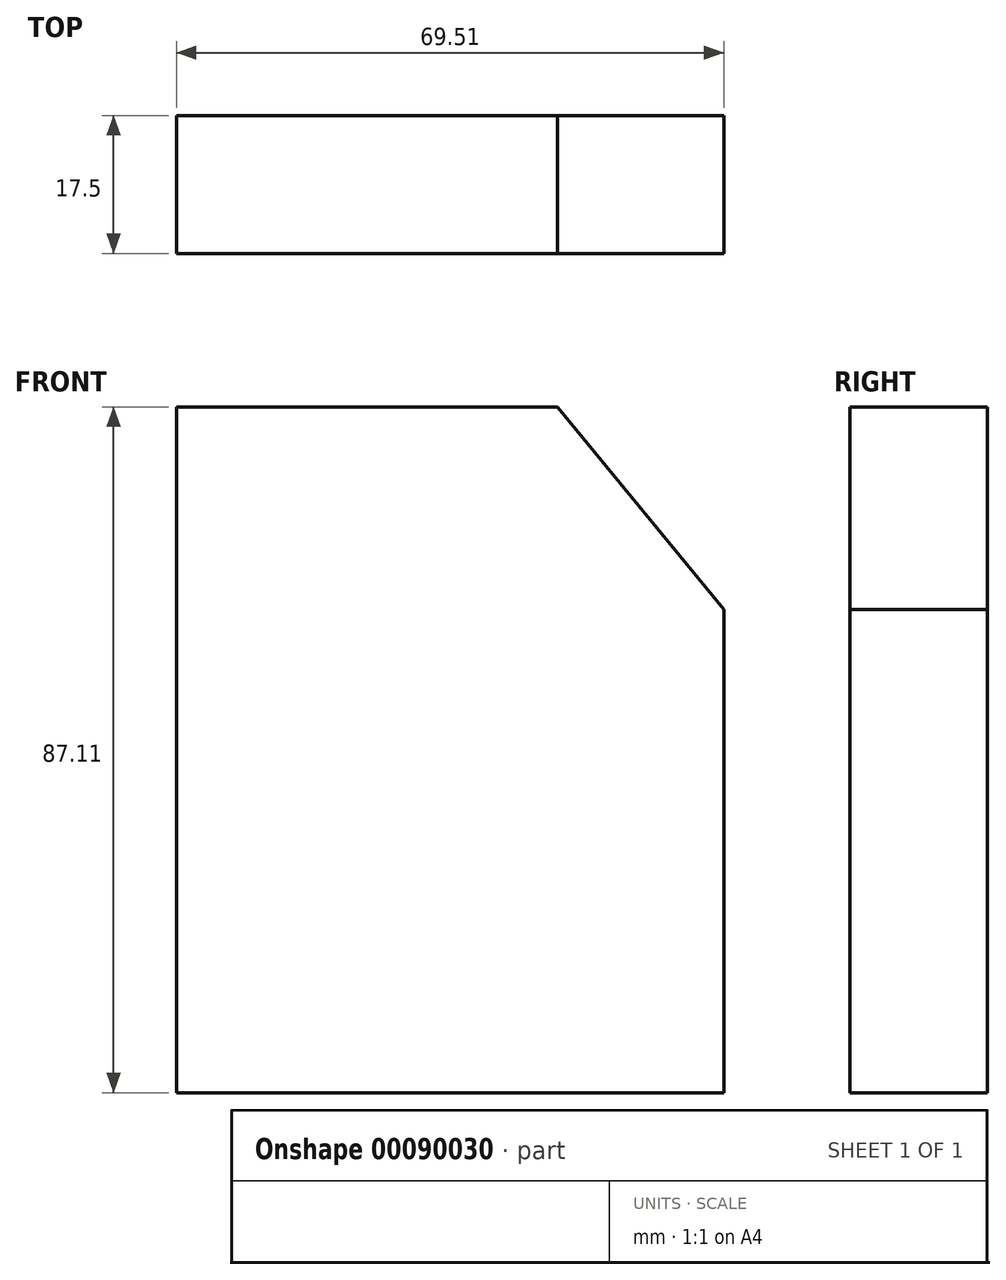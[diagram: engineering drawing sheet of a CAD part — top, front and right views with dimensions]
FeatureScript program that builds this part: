
annotation { "Feature Type Name" : "Feature", "Feature Type Description" : "" }
export const myFeature = defineFeature(function(context is Context, id is Id, definition is map)
    precondition{}
    {
        {
            var Q0;
            Q0=qCreatedBy(makeId("Front.planeOp"),FACE);
            var sketch = newSketch(context, id + "F0", { "sketchPlane" : qUnion([Q0])});
            skLineSegment(sketch, "E0.bottom", {"start": v(-22.88, -50) * mm, "end": v(46.63, -50) * mm});
            skLineSegment(sketch, "E0.top", {"start": v(-22.88, 37.1) * mm, "end": v(46.63, 37.1) * mm});
            skLineSegment(sketch, "E0.left", {"start": v(-22.88, -50) * mm, "end": v(-22.88, 37.1) * mm});
            skLineSegment(sketch, "E0.right", {"start": v(46.63, -50) * mm, "end": v(46.63, 37.1) * mm});
            skLineSegment(sketch, "E1", {"start": v(25.5, 37.1) * mm, "end": v(46.63, 11.37) * mm});
            skSolve(sketch);
        }
        {
            var Q0;
            {var subQ1=sQuery(id+"F0.wireOp",EDGE,"E0.bottom");Q0=makeQuery(id+"F0.imprint","IMPRINT",FACE,{"disambiguationData":[TD([[makeQuery(id+"F0.imprint","IMPRINT",EDGE,{"derivedFrom":subQ1}),1.0]])]});}
            extrude(context, id + "F1", {"entities" : qUnion([Q0]), "endBound" : BoundingType.SYMMETRIC, "depth" : 10 * mm});
        }
        {
            var Q0;
            Q0=makeQuery(id+"F1.opExtrude","CAP_FACE",FACE,{"disambiguationData":[OSD([sQuery(id+"F0.wireOp",EDGE,"E0.bottom"),sQuery(id+"F0.wireOp",EDGE,"E0.top"),sQuery(id+"F0.wireOp",EDGE,"E0.left"),sQuery(id+"F0.wireOp",EDGE,"E0.right"),sQuery(id+"F0.wireOp",EDGE,"E1")])],"isStart":false});
            extrude(context, id + "F2", {"entities" : qUnion([Q0]), "operationType" : NewBodyOperationType.ADD, "endBound" : BoundingType.SYMMETRIC, "depth" : 15 * mm});
        }
    });
